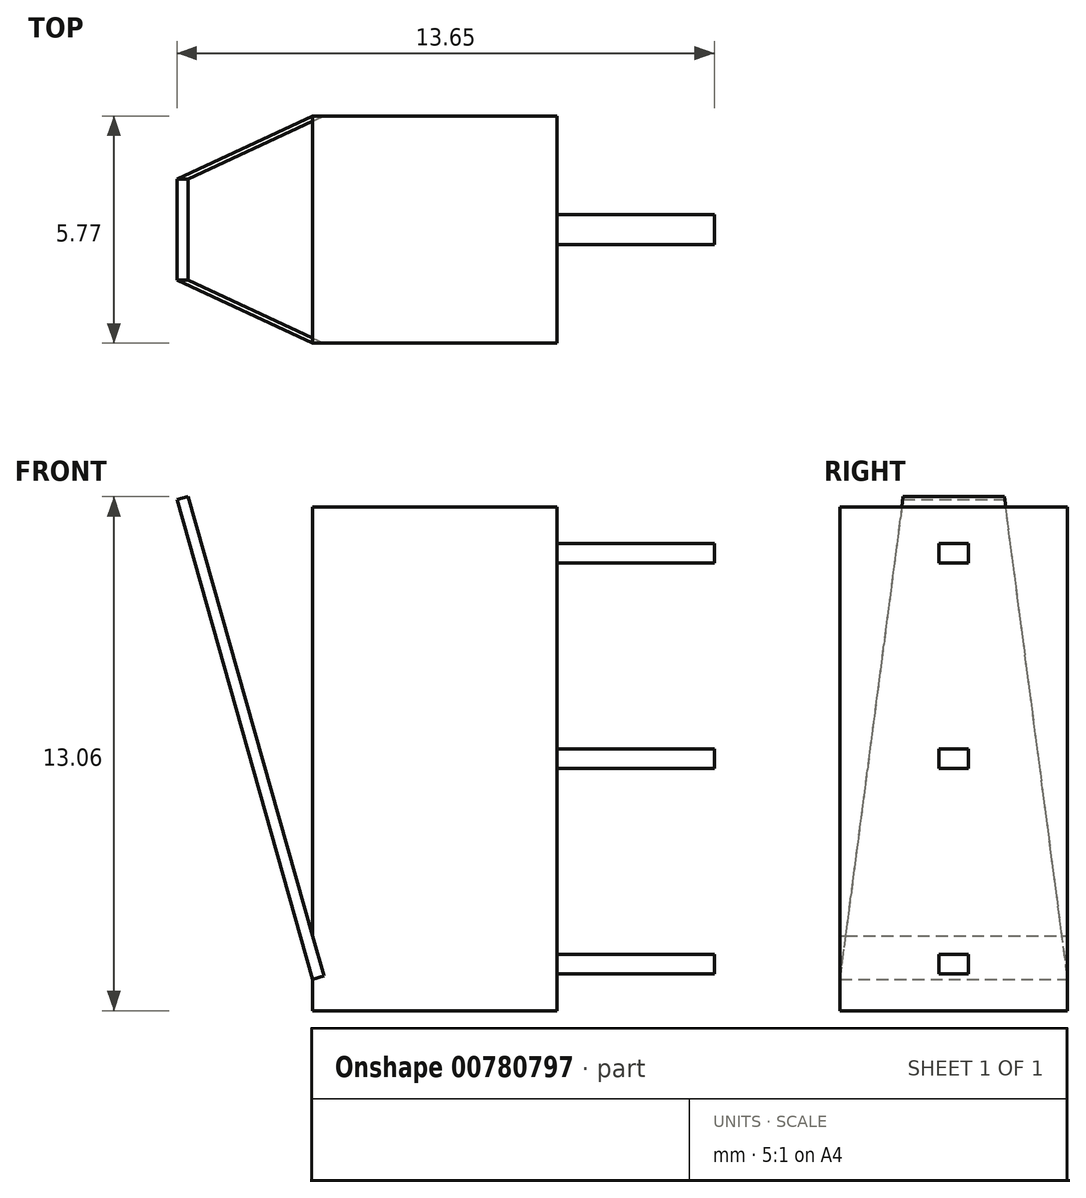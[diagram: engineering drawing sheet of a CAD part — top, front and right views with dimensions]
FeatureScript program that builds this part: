
annotation { "Feature Type Name" : "Feature", "Feature Type Description" : "" }
export const myFeature = defineFeature(function(context is Context, id is Id, definition is map)
    precondition{}
    {
        {
            var Q0;
            Q0=qCreatedBy(makeId("Front.planeOp"),FACE);
            var sketch = newSketch(context, id + "F0", { "sketchPlane" : qUnion([Q0])});
            skLineSegment(sketch, "E0.bottom", {"start": v(3.1, 6.4) * mm, "end": v(-3.1, 6.4) * mm});
            skLineSegment(sketch, "E0.top", {"start": v(3.1, -6.4) * mm, "end": v(-3.1, -6.4) * mm});
            skLineSegment(sketch, "E0.left", {"start": v(3.1, 6.4) * mm, "end": v(3.1, -6.4) * mm});
            skLineSegment(sketch, "E0.right", {"start": v(-3.1, 6.4) * mm, "end": v(-3.1, -6.4) * mm});
            skPoint(sketch, "E0.middle", {"position": v(0, 0) * mm});
            skSolve(sketch);
        }
        {
            var Q0;
            Q0=qSketchRegion(id+"F0",true);
            extrude(context, id + "F1", {"entities" : qUnion([Q0]), "depth" : 5.77 * mm, "offsetDistance" : 25.4 * mm});
        }
        {
            var Q0;
            Q0=makeQuery(id+"F1.opExtrude","SWEPT_FACE",FACE,{"disambiguationData":[OSD([sQuery(id+"F0.wireOp",EDGE,"E0.left")])]});
            var sketch = newSketch(context, id + "F2", { "sketchPlane" : qUnion([Q0])});
            skLineSegment(sketch, "E1", {"start": v(-2.88, 0) * mm, "end": v(-2.89, 5.47) * mm, "construction": true});
            skLineSegment(sketch, "E2", {"start": v(-5.77, 0) * mm, "end": v(0, 0) * mm, "construction": true});
            skLineSegment(sketch, "E3.bottom", {"start": v(-2.89, 5.47) * mm, "end": v(-2.5, 5.47) * mm});
            skLineSegment(sketch, "E3.top", {"start": v(-2.88, 4.97) * mm, "end": v(-2.5, 4.97) * mm});
            skLineSegment(sketch, "E3.left", {"start": v(-2.89, 5.47) * mm, "end": v(-2.89, 4.97) * mm});
            skLineSegment(sketch, "E3.right", {"start": v(-2.5, 5.47) * mm, "end": v(-2.5, 4.97) * mm});
            skLineSegment(sketch, "E4.bottom", {"start": v(-2.51, 0.25) * mm, "end": v(-3.26, 0.25) * mm});
            skLineSegment(sketch, "E4.top", {"start": v(-2.51, -0.25) * mm, "end": v(-3.26, -0.25) * mm});
            skLineSegment(sketch, "E4.left", {"start": v(-2.51, 0.25) * mm, "end": v(-2.51, -0.25) * mm});
            skLineSegment(sketch, "E4.right", {"start": v(-3.26, 0.25) * mm, "end": v(-3.26, -0.25) * mm});
            skPoint(sketch, "E4.middle", {"position": v(-2.88, 0) * mm});
            skLineSegment(sketch, "E5.MirrorCS", {"start": v(-3.26, 5.47) * mm, "end": v(-3.26, 4.97) * mm});
            skLineSegment(sketch, "E6.MirrorCS", {"start": v(-2.89, 4.97) * mm, "end": v(-3.26, 4.97) * mm});
            skLineSegment(sketch, "E7.MirrorCS", {"start": v(-2.89, 5.47) * mm, "end": v(-3.26, 5.47) * mm});
            skLineSegment(sketch, "E8.MirrorCS", {"start": v(-2.51, 0.25) * mm, "end": v(-2.5, -0.25) * mm});
            skLineSegment(sketch, "E9.MirrorCS", {"start": v(-3.26, 0.25) * mm, "end": v(-2.51, 0.25) * mm});
            skLineSegment(sketch, "E10.MirrorCS", {"start": v(-3.26, -0.25) * mm, "end": v(-2.51, -0.25) * mm});
            skLineSegment(sketch, "E11.MirrorCS", {"start": v(0, 0) * mm, "end": v(-5.77, 0) * mm, "construction": true});
            skLineSegment(sketch, "E12.MirrorCS", {"start": v(-2.89, -5.47) * mm, "end": v(-2.89, -4.97) * mm});
            skLineSegment(sketch, "E13.MirrorCS", {"start": v(-2.51, -0.25) * mm, "end": v(-2.51, 0.25) * mm});
            skLineSegment(sketch, "E14.MirrorCS", {"start": v(-3.26, -0.25) * mm, "end": v(-3.26, 0.25) * mm});
            skLineSegment(sketch, "E15.MirrorCS", {"start": v(-3.26, -5.47) * mm, "end": v(-3.26, -4.97) * mm});
            skLineSegment(sketch, "E16.MirrorCS", {"start": v(-2.5, -5.47) * mm, "end": v(-2.5, -4.97) * mm});
            skLineSegment(sketch, "E17.MirrorCS", {"start": v(-2.89, -4.97) * mm, "end": v(-3.26, -4.97) * mm});
            skLineSegment(sketch, "E18.MirrorCS", {"start": v(-2.88, -4.97) * mm, "end": v(-2.5, -4.97) * mm});
            skLineSegment(sketch, "E19.MirrorCS", {"start": v(-2.89, -5.47) * mm, "end": v(-3.26, -5.47) * mm});
            skLineSegment(sketch, "E20.MirrorCS", {"start": v(-2.89, -5.47) * mm, "end": v(-2.5, -5.47) * mm});
            skLineSegment(sketch, "E21.MirrorCS", {"start": v(-2.51, -0.25) * mm, "end": v(-2.5, 0.25) * mm});
            skSolve(sketch);
        }
        {
            var Q0;
            Q0=qSketchRegion(id+"F2",true);
            extrude(context, id + "F3", {"entities" : qUnion([Q0]), "operationType" : NewBodyOperationType.ADD, "depth" : 4 * mm, "offsetDistance" : 25 * mm});
        }
        {
            var Q0;
            Q0=makeQuery(id+"F1.opExtrude","CAP_FACE",FACE,{"disambiguationData":[OSD([sQuery(id+"F0.wireOp",EDGE,"E0.bottom"),sQuery(id+"F0.wireOp",EDGE,"E0.top"),sQuery(id+"F0.wireOp",EDGE,"E0.left"),sQuery(id+"F0.wireOp",EDGE,"E0.right")])],"isStart":false});
            var sketch = newSketch(context, id + "F4", { "sketchPlane" : qUnion([Q0])});
            skLineSegment(sketch, "E22", {"start": v(-3.1, -5.6) * mm, "end": v(-6.55, 6.58) * mm});
            skSolve(sketch);
        }
        {
            var Q0;
            Q0=qSketchRegion(id+"F4",true);
            var Q1;
            Q1=sQuery(id+"F4.wireOp",EDGE,"E22");
            var Q2;
            Q2=makeQuery(id+"F1.opExtrude","CAP_FACE",FACE,{"disambiguationData":[OSD([sQuery(id+"F0.wireOp",EDGE,"E0.bottom"),sQuery(id+"F0.wireOp",EDGE,"E0.top"),sQuery(id+"F0.wireOp",EDGE,"E0.left"),sQuery(id+"F0.wireOp",EDGE,"E0.right")])],"isStart":true});
            extrude(context, id + "F5", {"entities" : qUnion([Q0]), "bodyType" : ToolBodyType.SURFACE, "surfaceEntities" : qUnion([Q1]), "endBound" : BoundingType.UP_TO_SURFACE, "oppositeDirection" : true, "depth" : 25 * mm, "endBoundEntityFace" : qUnion([Q2]), "offsetDistance" : 25 * mm});
        }
        {
            var Q0;
            Q0=makeQuery(id+"F5.opExtrude","SWEPT_FACE",FACE,{"disambiguationData":[OSD([sQuery(id+"F4.wireOp",EDGE,"E22")])]});
            var sketch = newSketch(context, id + "F6", { "sketchPlane" : qUnion([Q0])});
            skLineSegment(sketch, "E23.bottom", {"start": v(0, 8.12) * mm, "end": v(5.77, 8.12) * mm});
            skLineSegment(sketch, "E23.top", {"start": v(0, -4.54) * mm, "end": v(5.77, -4.54) * mm});
            skLineSegment(sketch, "E23.left", {"start": v(0, 8.12) * mm, "end": v(0, -4.54) * mm});
            skLineSegment(sketch, "E23.right", {"start": v(5.77, 8.12) * mm, "end": v(5.77, -4.54) * mm});
            skSolve(sketch);
        }
        {
            var Q0;
            Q0=qSketchRegion(id+"F6",true);
            extrude(context, id + "F7", {"entities" : qUnion([Q0]), "operationType" : NewBodyOperationType.ADD, "oppositeDirection" : true, "depth" : .3 * mm, "offsetDistance" : 25 * mm});
        }
        {
            var Q0;
            Q0=makeQuery(id+"F7.opExtrude","CAP_FACE",FACE,{"disambiguationData":[OSD([sQuery(id+"F6.wireOp",EDGE,"E23.bottom"),sQuery(id+"F6.wireOp",EDGE,"E23.top"),sQuery(id+"F6.wireOp",EDGE,"E23.left"),sQuery(id+"F6.wireOp",EDGE,"E23.right")])],"isStart":true});
            var sketch = newSketch(context, id + "F8", { "sketchPlane" : qUnion([Q0])});
            skLineSegment(sketch, "E24", {"start": v(5.77, -4.54) * mm, "end": v(4.17, 8.12) * mm});
            skLineSegment(sketch, "E25", {"start": v(4.17, 8.12) * mm, "end": v(1.6, 8.12) * mm});
            skLineSegment(sketch, "E26", {"start": v(1.6, 8.12) * mm, "end": v(0, -4.54) * mm});
            skLineSegment(sketch, "E27", {"start": v(1.6, 8.12) * mm, "end": v(0, 8.12) * mm});
            skLineSegment(sketch, "E28", {"start": v(0, 8.12) * mm, "end": v(0, -4.54) * mm});
            skLineSegment(sketch, "E29", {"start": v(5.77, -4.54) * mm, "end": v(5.77, 8.12) * mm});
            skLineSegment(sketch, "E30", {"start": v(5.77, 8.12) * mm, "end": v(4.17, 8.12) * mm});
            skSolve(sketch);
        }
        {
            var Q0;
            Q0=qSketchRegion(id+"F8",true);
            var Q1;
            Q1=makeQuery(id+"F7.opExtrude","CAP_FACE",FACE,{"disambiguationData":[OSD([sQuery(id+"F6.wireOp",EDGE,"E23.bottom"),sQuery(id+"F6.wireOp",EDGE,"E23.top"),sQuery(id+"F6.wireOp",EDGE,"E23.left"),sQuery(id+"F6.wireOp",EDGE,"E23.right")])],"isStart":false});
            extrude(context, id + "F9", {"entities" : qUnion([Q0]), "operationType" : NewBodyOperationType.REMOVE, "endBound" : BoundingType.UP_TO_SURFACE, "oppositeDirection" : true, "depth" : .3 * mm, "endBoundEntityFace" : qUnion([Q1]), "offsetDistance" : 25 * mm});
        }
    });
